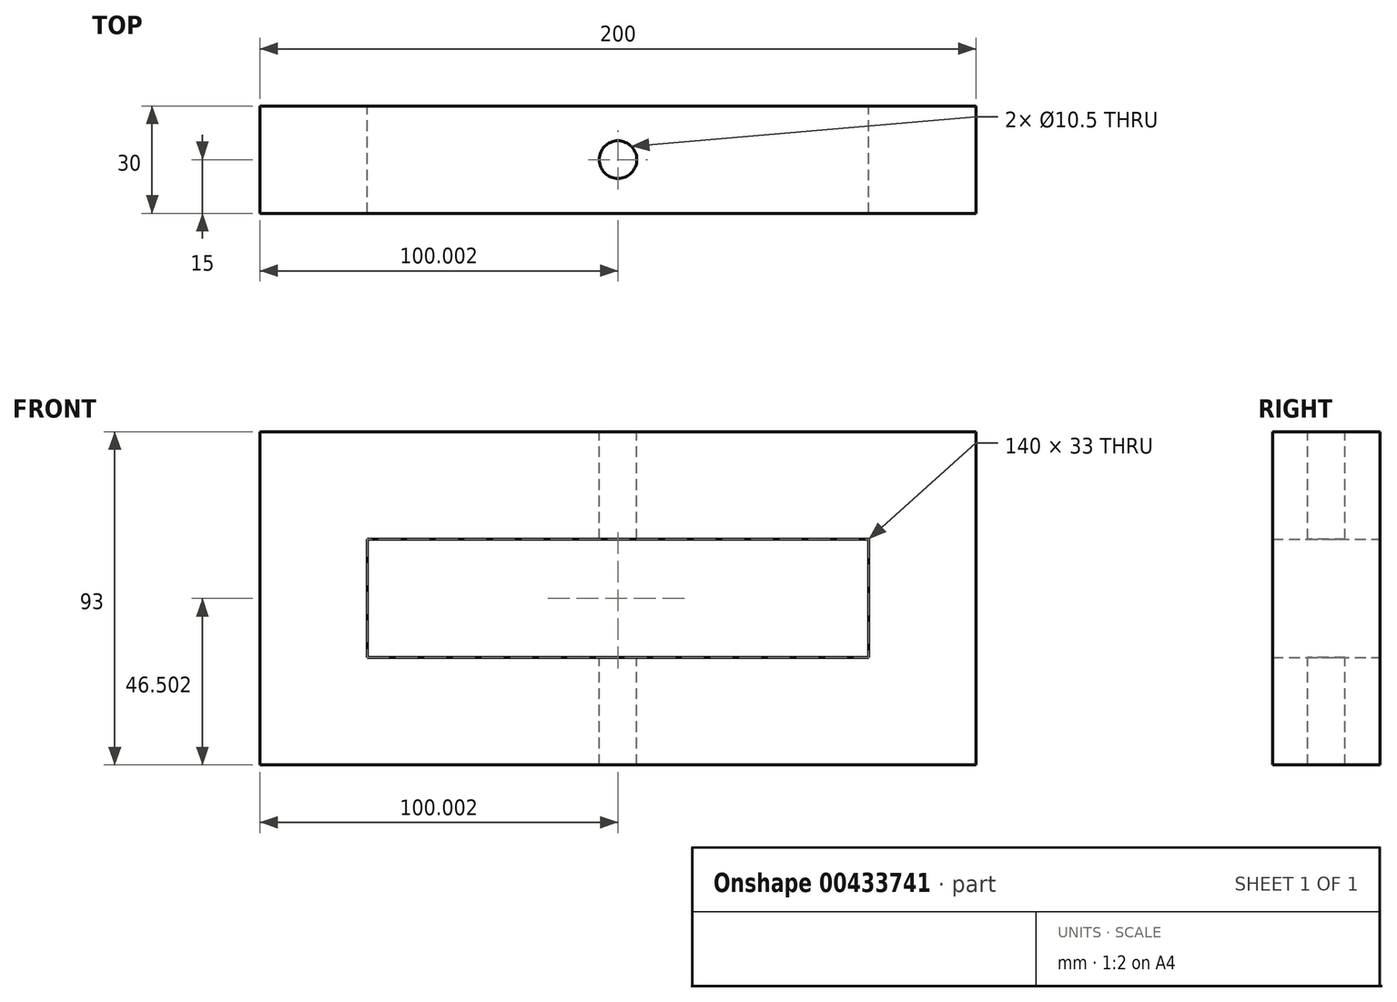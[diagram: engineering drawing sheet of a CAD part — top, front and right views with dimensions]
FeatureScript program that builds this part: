
annotation { "Feature Type Name" : "Feature", "Feature Type Description" : "" }
export const myFeature = defineFeature(function(context is Context, id is Id, definition is map)
    precondition{}
    {
        {
            var Q0;
            Q0=qCreatedBy(makeId("Front.planeOp"),FACE);
            var sketch = newSketch(context, id + "F0", { "sketchPlane" : qUnion([Q0])});
            skLineSegment(sketch, "E0.bottom", {"start": v(-95.19, 9.54) * mm, "end": v(104.81, 9.54) * mm});
            skLineSegment(sketch, "E0.top", {"start": v(-95.19, -20.46) * mm, "end": v(104.81, -20.46) * mm});
            skLineSegment(sketch, "E0.left", {"start": v(-95.19, 9.54) * mm, "end": v(-95.19, -20.46) * mm});
            skLineSegment(sketch, "E0.right", {"start": v(104.81, 9.54) * mm, "end": v(104.81, -20.46) * mm});
            skLineSegment(sketch, "E1.bottom", {"start": v(-95.19, -20.46) * mm, "end": v(-65.19, -20.46) * mm});
            skLineSegment(sketch, "E1.top", {"start": v(-95.19, -53.46) * mm, "end": v(-65.19, -53.46) * mm});
            skLineSegment(sketch, "E1.left", {"start": v(-95.19, -20.46) * mm, "end": v(-95.19, -53.46) * mm});
            skLineSegment(sketch, "E1.right", {"start": v(-65.19, -20.46) * mm, "end": v(-65.19, -53.46) * mm});
            skLineSegment(sketch, "E2.bottom", {"start": v(-95.19, -53.46) * mm, "end": v(104.81, -53.46) * mm});
            skLineSegment(sketch, "E2.top", {"start": v(-95.19, -83.46) * mm, "end": v(104.81, -83.46) * mm});
            skLineSegment(sketch, "E2.left", {"start": v(-95.19, -53.46) * mm, "end": v(-95.19, -83.46) * mm});
            skLineSegment(sketch, "E2.right", {"start": v(104.81, -53.46) * mm, "end": v(104.81, -83.46) * mm});
            skLineSegment(sketch, "E3.bottom", {"start": v(104.81, -20.46) * mm, "end": v(74.81, -20.46) * mm});
            skLineSegment(sketch, "E3.top", {"start": v(104.81, -53.46) * mm, "end": v(74.81, -53.46) * mm});
            skLineSegment(sketch, "E3.left", {"start": v(104.81, -20.46) * mm, "end": v(104.81, -53.46) * mm});
            skLineSegment(sketch, "E3.right", {"start": v(74.81, -20.46) * mm, "end": v(74.81, -53.46) * mm});
            skSolve(sketch);
        }
        {
            var Q0;
            Q0 = qSketchRegion(id + "F0", true);
            extrude(context, id + "F1", {"entities" : qUnion([Q0]), "depth" : 30 * mm, "offsetDistance" : 25 * mm});
        }
        {
            var Q0;
            Q0=makeQuery(id+"F1.opExtrude","SWEPT_FACE",FACE,{"disambiguationData":[OSD([sQuery(id+"F0.wireOp",EDGE,"E0.bottom")])]});
            var sketch = newSketch(context, id + "F2", { "sketchPlane" : qUnion([Q0])});
            skCircle(sketch, "E4", {"center": v(4.81, -15) * mm, "radius": 5.5 * mm});
            skSolve(sketch);
        }
        {
            var Q0;
            Q0=sQuery(id+"F2.wireOp",VERTEX,"E4.center");
            var Q1;
            Q1=makeQuery(id+"F1.opExtrude","SWEPT_BODY",BODY,{"disambiguationData":[OSD([sQuery(id+"F0.wireOp",EDGE,"E0.bottom"),sQuery(id+"F0.wireOp",EDGE,"E0.top"),sQuery(id+"F0.wireOp",EDGE,"E0.left"),sQuery(id+"F0.wireOp",EDGE,"E0.right"),sQuery(id+"F0.wireOp",EDGE,"E1.left"),sQuery(id+"F0.wireOp",EDGE,"E1.right"),sQuery(id+"F0.wireOp",EDGE,"E2.bottom"),sQuery(id+"F0.wireOp",EDGE,"E2.top"),sQuery(id+"F0.wireOp",EDGE,"E2.left"),sQuery(id+"F0.wireOp",EDGE,"E2.right"),sQuery(id+"F0.wireOp",EDGE,"E3.left"),sQuery(id+"F0.wireOp",EDGE,"E3.right")])]});
            hole(context, id + "F3", {"style" : HoleStyle.SIMPLE, "endStyle" : HoleEndStyle.THROUGH, "holeDiameter" : 10.5 * mm, "majorDiameter" : 5 * mm, "isTappedThrough" : true, "tappedDepth" : 12 * mm, "tapClearance" : 3, "locations" : qUnion([Q0]), "scope" : qUnion([Q1])});
        }
    });
